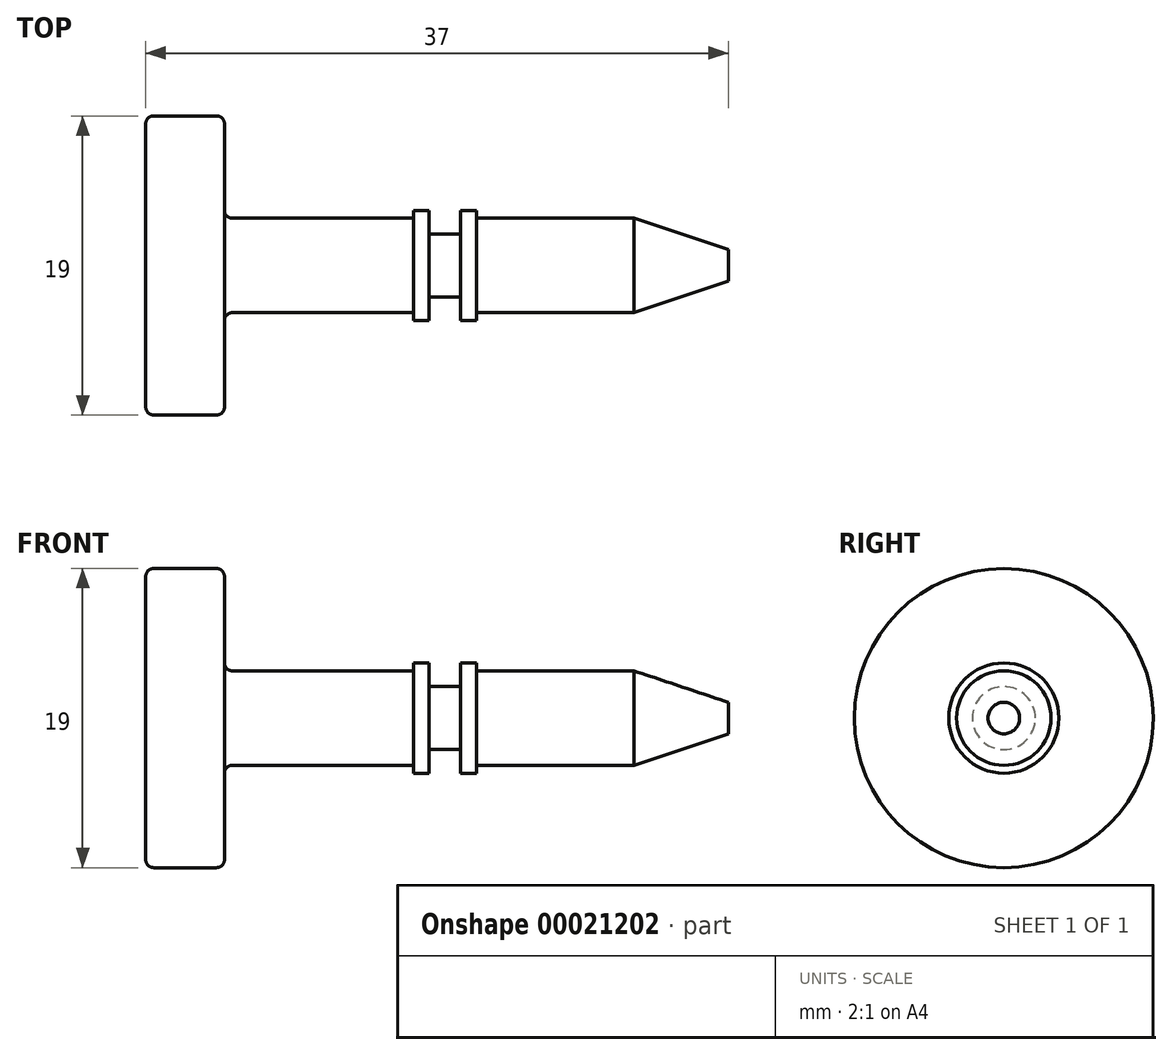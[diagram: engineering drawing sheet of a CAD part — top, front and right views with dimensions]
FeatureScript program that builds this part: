
annotation { "Feature Type Name" : "Feature", "Feature Type Description" : "" }
export const myFeature = defineFeature(function(context is Context, id is Id, definition is map)
    precondition{}
    {
        {
            var Q0;
            Q0=qCreatedBy(makeId("Front.planeOp"),FACE);
            var sketch = newSketch(context, id + "F0", { "sketchPlane" : qUnion([Q0])});
            skLineSegment(sketch, "E0", {"start": v(0, 0) * mm, "end": v(37, 0) * mm});
            skLineSegment(sketch, "E1", {"start": v(37, 0) * mm, "end": v(37, 1) * mm});
            skLineSegment(sketch, "E2", {"start": v(37, 1) * mm, "end": v(31, 3) * mm});
            skLineSegment(sketch, "E3", {"start": v(31, 3) * mm, "end": v(21, 3) * mm});
            skLineSegment(sketch, "E4", {"start": v(21, 3) * mm, "end": v(21, 3.5) * mm});
            skLineSegment(sketch, "E5", {"start": v(21, 3.5) * mm, "end": v(20, 3.5) * mm});
            skLineSegment(sketch, "E6", {"start": v(20, 3.5) * mm, "end": v(20, 2) * mm});
            skLineSegment(sketch, "E7", {"start": v(20, 2) * mm, "end": v(18, 2) * mm});
            skLineSegment(sketch, "E8", {"start": v(18, 2) * mm, "end": v(18, 3.5) * mm});
            skLineSegment(sketch, "E9", {"start": v(18, 3.5) * mm, "end": v(17, 3.5) * mm});
            skLineSegment(sketch, "E10", {"start": v(17, 3.5) * mm, "end": v(17, 3) * mm});
            skLineSegment(sketch, "E11", {"start": v(17, 3) * mm, "end": v(5, 3) * mm});
            skLineSegment(sketch, "E12", {"start": v(5, 3) * mm, "end": v(5, 9.5) * mm});
            skLineSegment(sketch, "E13", {"start": v(5, 9.5) * mm, "end": v(0, 9.5) * mm});
            skLineSegment(sketch, "E14", {"start": v(0, 9.5) * mm, "end": v(0, 0) * mm});
            skSolve(sketch);
        }
        {
            var Q0;
            Q0=qSketchRegion(id+"F0",true);
            var Q1;
            Q1=sQuery(id+"F0.wireOp",EDGE,"E0");
            revolve(context, id + "F1", {"entities" : qUnion([Q0]), "axis" : qUnion([Q1]), "revolveType" : RevolveType.FULL});
        }
        {
            var Q0;
            Q0=makeQuery(id+"F1.opRevolve","SWEPT_EDGE",EDGE,{"disambiguationData":[OSD([sQuery(id+"F0.wireOp",EDGE,"E13"),sQuery(id+"F0.wireOp",EDGE,"E14")])]});
            var Q1;
            Q1=makeQuery(id+"F1.opRevolve","SWEPT_EDGE",EDGE,{"disambiguationData":[OSD([sQuery(id+"F0.wireOp",EDGE,"E12"),sQuery(id+"F0.wireOp",EDGE,"E13")])]});
            var Q2;
            Q2=makeQuery(id+"F1.opRevolve","SWEPT_EDGE",EDGE,{"disambiguationData":[OSD([sQuery(id+"F0.wireOp",EDGE,"E11"),sQuery(id+"F0.wireOp",EDGE,"E12")])]});
            fillet(context, id + "F2", {"entities" : qUnion([Q0, Q1, Q2]), "radius" : 0.5 * mm, "tangentPropagation" : true, "allowEdgeOverflow" : false});
        }
    });
